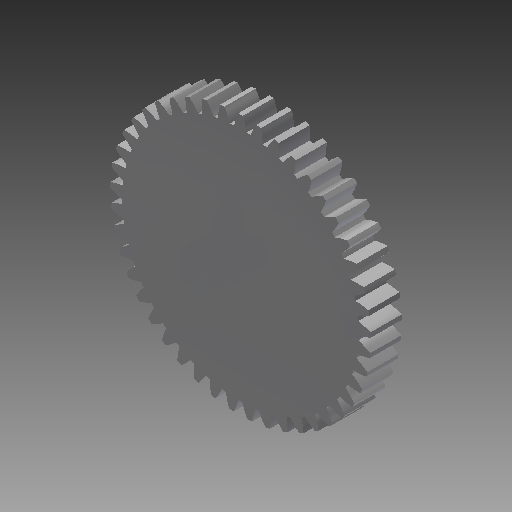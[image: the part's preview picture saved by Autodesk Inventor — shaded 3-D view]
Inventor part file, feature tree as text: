
AUTODESK INVENTOR PART (.ipt)
format: ipt  version: 2019 (Build 230136000, 136)  size: 327,168 bytes
history: native  units: mm (DEFAULTED — no unit token found)
features: plane x3, other x3, sketch x2, extrude x1
ambient origin geometry x8: Origin, YZ Plane, XZ Plane, XY Plane, X Axis, Y Axis, Z Axis, Center Point
bodies: Solid1 (feature_tree)
feature tree (9):
  extrude  "Extrusion1"  Depth=1.25mm TaperAngle=0.0deg
  plane  "Work Plane2"
  plane  "Work Plane8"
  plane  "Work Plane9"
  other  "Spur Gear"
  sketch  "Sketch1"  dims[d0=10.46mm d1=1.25mm d2=0.0mm]
  sketch  "Sketch2"  dims[d3=10.0mm d4=10.0mm d5=0.0mm d16=6.0mm d17=0.0mm d34=0.698132mm d39=0.0mm d41=0.0mm d43=6.0mm d46=6.0mm d47=0.0mm d48=0.0mm]
  other  "Srf1"
  other  "Pitch Diameter"
